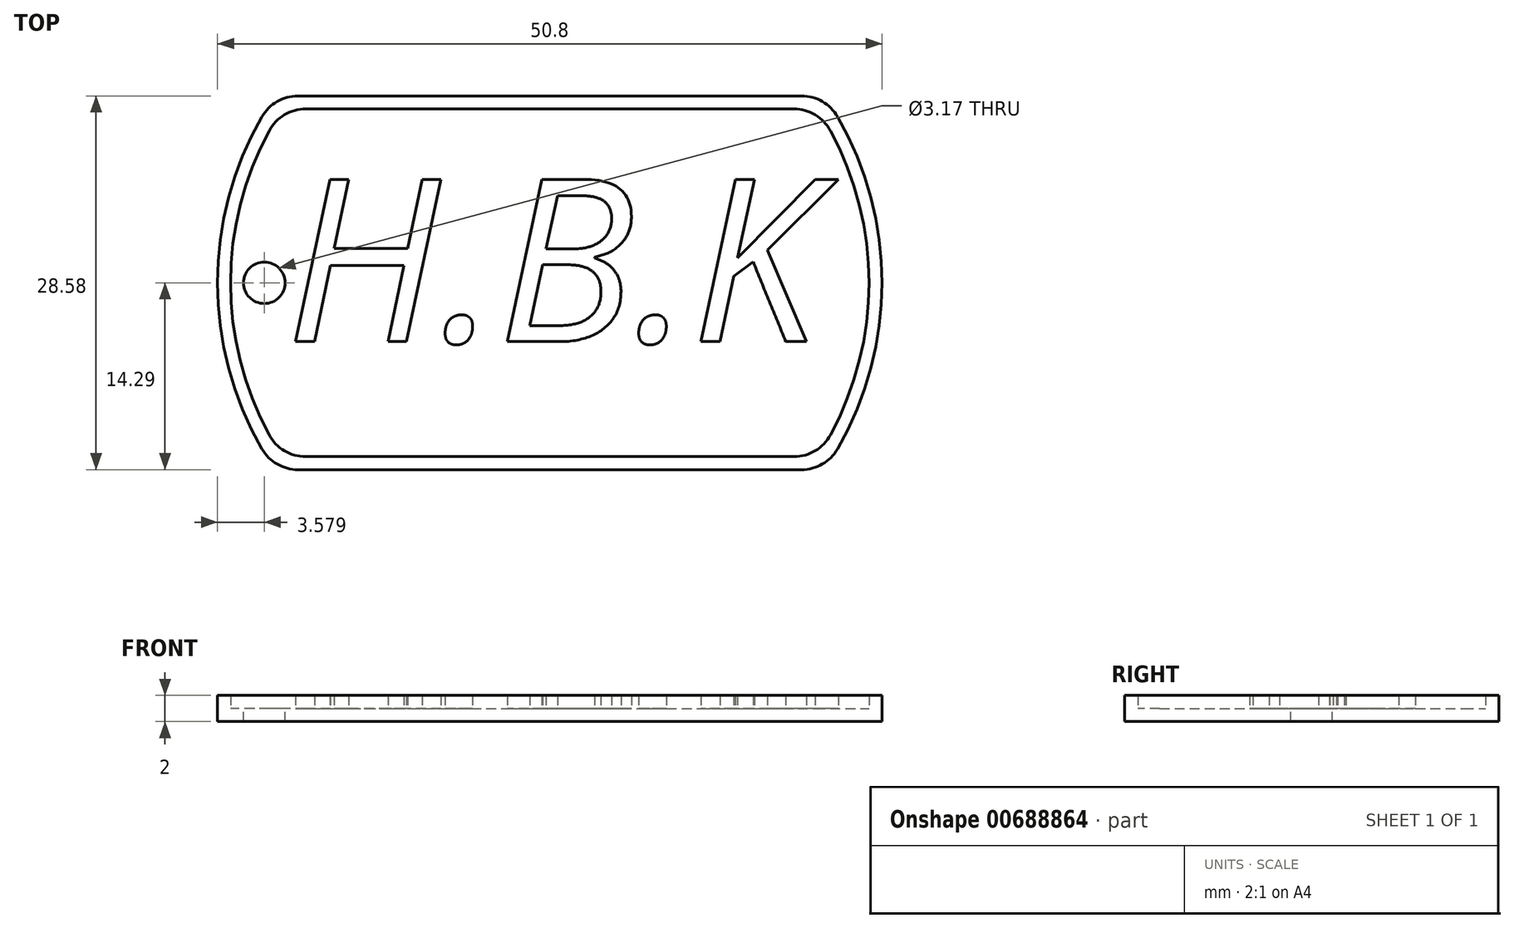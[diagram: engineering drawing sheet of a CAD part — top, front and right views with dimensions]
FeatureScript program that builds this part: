
annotation { "Feature Type Name" : "Feature", "Feature Type Description" : "" }
export const myFeature = defineFeature(function(context is Context, id is Id, definition is map)
    precondition{}
    {
        {
            var Q0;
            Q0=qCreatedBy(makeId("Top.planeOp"),FACE);
            var sketch = newSketch(context, id + "F0", { "sketchPlane" : qUnion([Q0])});
            skArc(sketch, "E0", {"start": v(-22, 12.7) * mm, "mid": v(-25.4, 0) * mm, "end": v(-22, -12.7) * mm});
            skLineSegment(sketch, "E1.top", {"start": v(-19.25, -14.29) * mm, "end": v(19.25, -14.29) * mm});
            skArc(sketch, "E2.trimOffspring", {"start": v(22, -12.7) * mm, "mid": v(25.4, 0) * mm, "end": v(22, 12.7) * mm});
            skLineSegment(sketch, "E3", {"start": v(-19.25, 14.29) * mm, "end": v(19.25, 14.29) * mm});
            skPoint(sketch, "E4.visualSharp", {"position": v(-21, 14.29) * mm});
            skArc(sketch, "E4.filletArc", {"start": v(-19.25, 14.29) * mm, "mid": v(-20.83, 13.86) * mm, "end": v(-22, 12.7) * mm});
            skPoint(sketch, "E5.visualSharp", {"position": v(21, 14.29) * mm});
            skArc(sketch, "E5.filletArc", {"start": v(22, 12.7) * mm, "mid": v(20.83, 13.86) * mm, "end": v(19.25, 14.29) * mm});
            skPoint(sketch, "E6.visualSharp", {"position": v(21, -14.29) * mm});
            skArc(sketch, "E6.filletArc", {"start": v(19.25, -14.29) * mm, "mid": v(20.83, -13.86) * mm, "end": v(22, -12.7) * mm});
            skPoint(sketch, "E7.visualSharp", {"position": v(-21, -14.29) * mm});
            skArc(sketch, "E7.filletArc", {"start": v(-22, -12.7) * mm, "mid": v(-20.83, -13.86) * mm, "end": v(-19.25, -14.29) * mm});
            skSolve(sketch);
        }
        {
            var Q0;
            Q0=makeQuery(id+"F0.imprint","IMPRINT",FACE,{"disambiguationData":[TD([[makeQuery(id+"F0.imprint","IMPRINT",EDGE,{"derivedFrom":sQuery(id+"F0.wireOp",EDGE,"E0")}),1.0]])]});
            extrude(context, id + "F1", {"entities" : qUnion([Q0]), "depth" : 1 * mm, "offsetDistance" : 25.4 * mm});
        }
        {
            var Q0;
            Q0=makeQuery(id+"F1.opExtrude","CAP_FACE",FACE,{"disambiguationData":[OSD([sQuery(id+"F0.wireOp",EDGE,"E0"),sQuery(id+"F0.wireOp",EDGE,"E1.top"),sQuery(id+"F0.wireOp",EDGE,"E2.trimOffspring"),sQuery(id+"F0.wireOp",EDGE,"E3"),sQuery(id+"F0.wireOp",EDGE,"E4.filletArc"),sQuery(id+"F0.wireOp",EDGE,"E5.filletArc"),sQuery(id+"F0.wireOp",EDGE,"E6.filletArc"),sQuery(id+"F0.wireOp",EDGE,"E7.filletArc")])],"isStart":false});
            var sketch = newSketch(context, id + "F2", { "sketchPlane" : qUnion([Q0])});
            skLineSegment(sketch, "E8.0", {"start": v(-18.66, 13.29) * mm, "end": v(18.66, 13.29) * mm});
            skArc(sketch, "E8.1", {"start": v(-21.45, 11.63) * mm, "mid": v(-24.4, 0) * mm, "end": v(-21.45, -11.63) * mm});
            skLineSegment(sketch, "E8.2", {"start": v(-18.66, -13.29) * mm, "end": v(18.66, -13.29) * mm});
            skArc(sketch, "E8.3", {"start": v(21.45, -11.63) * mm, "mid": v(24.4, 0) * mm, "end": v(21.45, 11.63) * mm});
            skPoint(sketch, "E9.visualSharp", {"position": v(-20.46, 13.29) * mm});
            skArc(sketch, "E9.filletArc", {"start": v(-18.66, 13.29) * mm, "mid": v(-20.29, 12.84) * mm, "end": v(-21.45, 11.63) * mm});
            skPoint(sketch, "E10.visualSharp", {"position": v(20.46, 13.29) * mm});
            skArc(sketch, "E10.filletArc", {"start": v(21.45, 11.63) * mm, "mid": v(20.29, 12.84) * mm, "end": v(18.66, 13.29) * mm});
            skPoint(sketch, "E11.visualSharp", {"position": v(20.46, -13.29) * mm});
            skArc(sketch, "E11.filletArc", {"start": v(18.66, -13.29) * mm, "mid": v(20.29, -12.84) * mm, "end": v(21.45, -11.63) * mm});
            skPoint(sketch, "E12.visualSharp", {"position": v(-20.46, -13.29) * mm});
            skArc(sketch, "E12.filletArc", {"start": v(-21.45, -11.63) * mm, "mid": v(-20.29, -12.84) * mm, "end": v(-18.66, -13.29) * mm});
            skLineSegment(sketch, "E13.0", {"start": v(-19.25, 14.29) * mm, "end": v(19.25, 14.29) * mm});
            skArc(sketch, "E13.1", {"start": v(-22, 12.7) * mm, "mid": v(-25.4, 0) * mm, "end": v(-22, -12.7) * mm});
            skLineSegment(sketch, "E13.2", {"start": v(-19.25, -14.29) * mm, "end": v(19.25, -14.29) * mm});
            skArc(sketch, "E13.3", {"start": v(22, -12.7) * mm, "mid": v(25.4, 0) * mm, "end": v(22, 12.7) * mm});
            skPoint(sketch, "E14.visualSharp", {"position": v(-21, -14.29) * mm});
            skArc(sketch, "E14.filletArc", {"start": v(-22, -12.7) * mm, "mid": v(-20.83, -13.86) * mm, "end": v(-19.25, -14.29) * mm});
            skPoint(sketch, "E15.visualSharp", {"position": v(21, -14.29) * mm});
            skArc(sketch, "E15.filletArc", {"start": v(19.25, -14.29) * mm, "mid": v(20.83, -13.86) * mm, "end": v(22, -12.7) * mm});
            skPoint(sketch, "E16.visualSharp", {"position": v(21, 14.29) * mm});
            skArc(sketch, "E16.filletArc", {"start": v(22, 12.7) * mm, "mid": v(20.83, 13.86) * mm, "end": v(19.25, 14.29) * mm});
            skPoint(sketch, "E17.visualSharp", {"position": v(-21, 14.29) * mm});
            skArc(sketch, "E17.filletArc", {"start": v(-19.25, 14.29) * mm, "mid": v(-20.83, 13.86) * mm, "end": v(-22, 12.7) * mm});
            skSolve(sketch);
        }
        {
            var Q0;
            Q0=makeQuery(id+"F2.imprint","IMPRINT",FACE,{"disambiguationData":[TD([[makeQuery(id+"F2.imprint","IMPRINT",EDGE,{"derivedFrom":sQuery(id+"F2.wireOp",EDGE,"E8.0")}),1.0]])]});
            extrude(context, id + "F3", {"entities" : qUnion([Q0]), "operationType" : NewBodyOperationType.ADD, "depth" : 1 * mm, "offsetDistance" : 25.4 * mm});
        }
        {
            var Q0;
            Q0=makeQuery(id+"F1.opExtrude","CAP_FACE",FACE,{"disambiguationData":[OSD([sQuery(id+"F0.wireOp",EDGE,"E0"),sQuery(id+"F0.wireOp",EDGE,"E1.top"),sQuery(id+"F0.wireOp",EDGE,"E2.trimOffspring"),sQuery(id+"F0.wireOp",EDGE,"E3"),sQuery(id+"F0.wireOp",EDGE,"E4.filletArc"),sQuery(id+"F0.wireOp",EDGE,"E5.filletArc"),sQuery(id+"F0.wireOp",EDGE,"E6.filletArc"),sQuery(id+"F0.wireOp",EDGE,"E7.filletArc")])],"isStart":false});
            var sketch = newSketch(context, id + "F4", { "sketchPlane" : qUnion([Q0])});
            skCircle(sketch, "E18", {"center": v(-21.82, 0) * mm, "radius": 1.59 * mm});
            skSolve(sketch);
        }
        {
            var Q0;
            Q0=makeQuery(id+"F4.imprint","IMPRINT",FACE,{"disambiguationData":[TD([[makeQuery(id+"F4.imprint","IMPRINT",EDGE,{"derivedFrom":sQuery(id+"F4.wireOp",EDGE,"E18")}),1.0]])]});
            extrude(context, id + "F5", {"entities" : qUnion([Q0]), "operationType" : NewBodyOperationType.REMOVE, "oppositeDirection" : true, "depth" : 1 * mm, "offsetDistance" : 25.4 * mm});
        }
        {
            var Q0;
            Q0=makeQuery(id+"F1.opExtrude","CAP_FACE",FACE,{"disambiguationData":[OSD([sQuery(id+"F0.wireOp",EDGE,"E0"),sQuery(id+"F0.wireOp",EDGE,"E1.top"),sQuery(id+"F0.wireOp",EDGE,"E2.trimOffspring"),sQuery(id+"F0.wireOp",EDGE,"E3"),sQuery(id+"F0.wireOp",EDGE,"E4.filletArc"),sQuery(id+"F0.wireOp",EDGE,"E5.filletArc"),sQuery(id+"F0.wireOp",EDGE,"E6.filletArc"),sQuery(id+"F0.wireOp",EDGE,"E7.filletArc")])],"isStart":false});
            var sketch = newSketch(context, id + "F6", { "sketchPlane" : qUnion([Q0])});
            skText(sketch, "E19", { "text": "H.B.K", "fontName": "OpenSans-Italic.ttf"});
            const initialGuessF6  = {"E19": [-0.02016, -0.0045, 1, 0, 0.01252]};
            skSetInitialGuess(sketch, initialGuessF6);
            skSolve(sketch);
        }
        {
            var Q0;
            Q0 = qSketchRegion(id + "F6", true);
            extrude(context, id + "F7", {"entities" : qUnion([Q0]), "operationType" : NewBodyOperationType.ADD, "depth" : 1 * mm, "offsetDistance" : 25.4 * mm});
        }
    });
